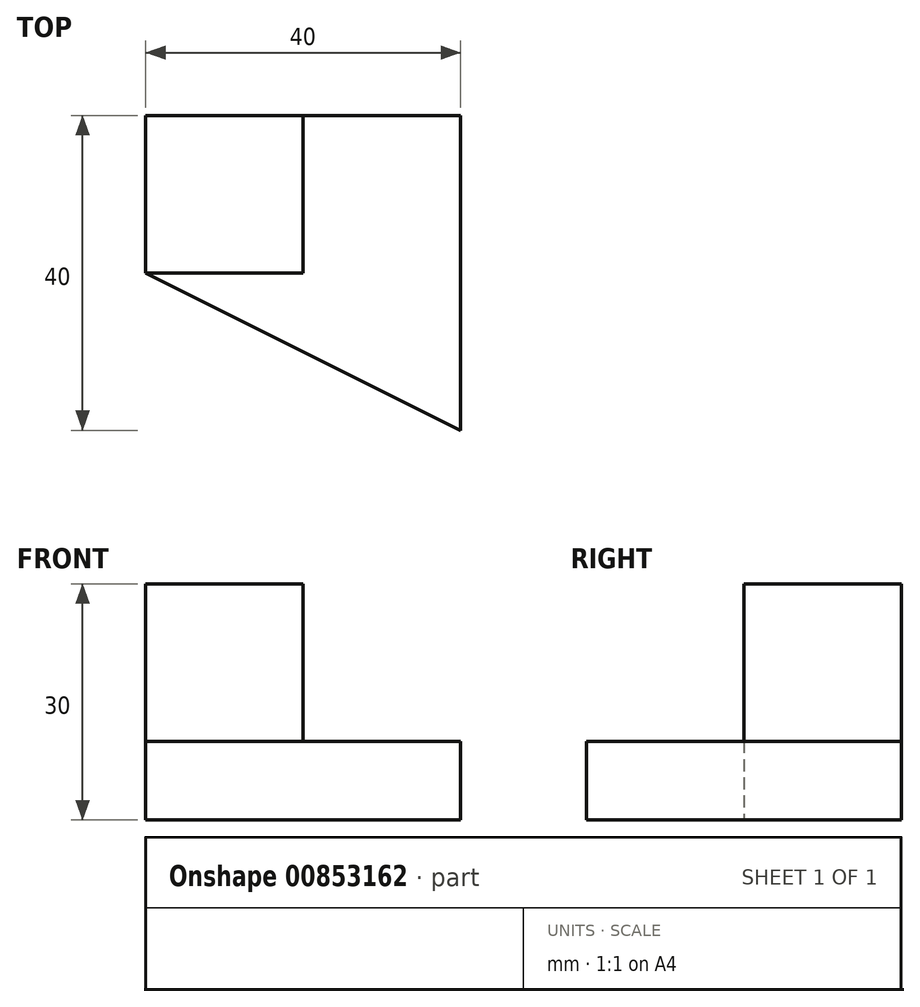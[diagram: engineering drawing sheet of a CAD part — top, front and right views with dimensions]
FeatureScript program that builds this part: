
annotation { "Feature Type Name" : "Feature", "Feature Type Description" : "" }
export const myFeature = defineFeature(function(context is Context, id is Id, definition is map)
    precondition{}
    {
        {
            var Q0;
            Q0=qCreatedBy(makeId("Top.planeOp"),FACE);
            var sketch = newSketch(context, id + "F0", { "sketchPlane" : qUnion([Q0])});
            skLineSegment(sketch, "E0.top", {"start": v(20, 20) * mm, "end": v(-20, 20) * mm});
            skLineSegment(sketch, "E0.left", {"start": v(20, -20) * mm, "end": v(20, 20) * mm});
            skLineSegment(sketch, "E0.right", {"start": v(-20, 0) * mm, "end": v(-20, 20) * mm});
            skPoint(sketch, "E0.middle", {"position": v(0, 0) * mm});
            skLineSegment(sketch, "E1", {"start": v(-20, 0) * mm, "end": v(20, -20) * mm});
            skPoint(sketch, "E0.bottom.end.orphan", {"position": v(-20, -20) * mm});
            skSolve(sketch);
        }
        {
            var Q0;
            Q0=makeQuery(id+"F0.imprint","IMPRINT",FACE,{"disambiguationData":[TD([[makeQuery(id+"F0.imprint","IMPRINT",EDGE,{"derivedFrom":sQuery(id+"F0.wireOp",EDGE,"E0.top")}),1.0]])]});
            extrude(context, id + "F1", {"entities" : qUnion([Q0]), "depth" : 10 * mm, "offsetDistance" : 25 * mm});
        }
        {
            var Q0;
            Q0=makeQuery(id+"F1.opExtrude","CAP_FACE",FACE,{"disambiguationData":[OSD([sQuery(id+"F0.wireOp",EDGE,"E0.top"),sQuery(id+"F0.wireOp",EDGE,"E0.left"),sQuery(id+"F0.wireOp",EDGE,"E0.right"),sQuery(id+"F0.wireOp",EDGE,"E1")])],"isStart":false});
            var sketch = newSketch(context, id + "F2", { "sketchPlane" : qUnion([Q0])});
            skLineSegment(sketch, "E2.bottom", {"start": v(-20, 20) * mm, "end": v(0, 20) * mm});
            skLineSegment(sketch, "E2.top", {"start": v(-20, 0) * mm, "end": v(0, 0) * mm});
            skLineSegment(sketch, "E2.left", {"start": v(-20, 20) * mm, "end": v(-20, 0) * mm});
            skLineSegment(sketch, "E2.right", {"start": v(0, 20) * mm, "end": v(0, 0) * mm});
            skSolve(sketch);
        }
        {
            var Q0;
            Q0=makeQuery(id+"F2.imprint","IMPRINT",FACE,{"disambiguationData":[TD([[makeQuery(id+"F2.imprint","IMPRINT",EDGE,{"derivedFrom":sQuery(id+"F2.wireOp",EDGE,"E2.bottom")}),1.0]])]});
            extrude(context, id + "F3", {"entities" : qUnion([Q0]), "operationType" : NewBodyOperationType.ADD, "depth" : 20 * mm, "offsetDistance" : 25 * mm});
        }
    });
